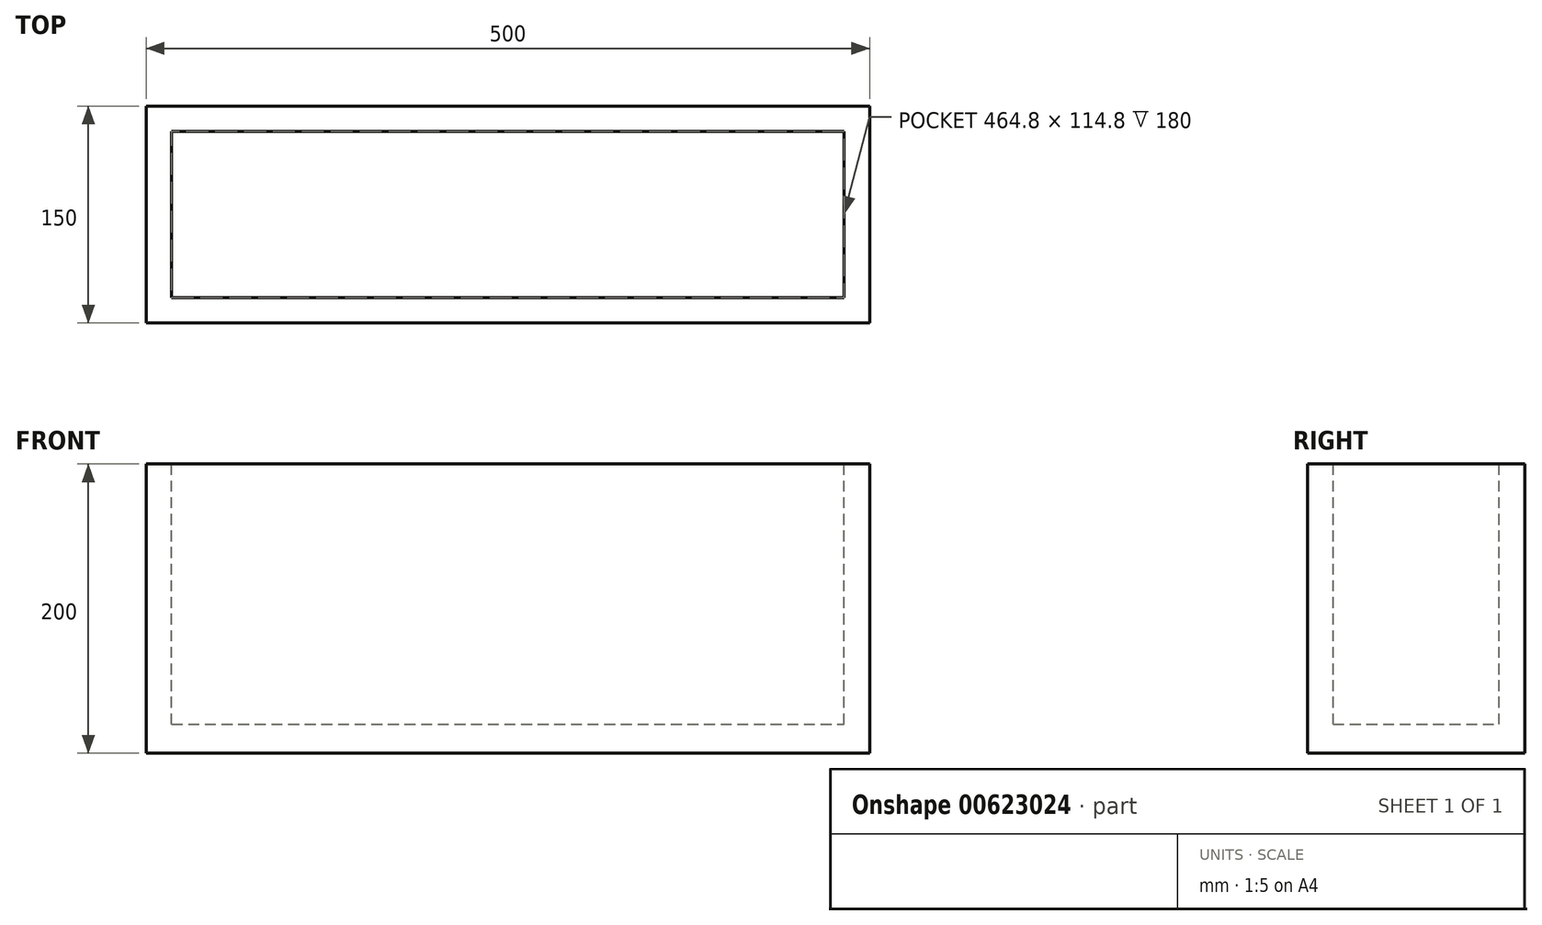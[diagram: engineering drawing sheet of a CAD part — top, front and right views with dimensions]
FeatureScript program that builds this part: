
annotation { "Feature Type Name" : "Feature", "Feature Type Description" : "" }
export const myFeature = defineFeature(function(context is Context, id is Id, definition is map)
    precondition{}
    {
        {
            var Q0;
            Q0=qCreatedBy(makeId("Top.planeOp"),FACE);
            var sketch = newSketch(context, id + "F0", { "sketchPlane" : qUnion([Q0])});
            skLineSegment(sketch, "E0.bottom", {"start": v(-187.75, -25.18) * mm, "end": v(312.25, -25.18) * mm});
            skLineSegment(sketch, "E0.top", {"start": v(-187.75, 124.82) * mm, "end": v(312.25, 124.82) * mm});
            skLineSegment(sketch, "E0.left", {"start": v(-187.75, -25.18) * mm, "end": v(-187.75, 124.82) * mm});
            skLineSegment(sketch, "E0.right", {"start": v(312.25, -25.18) * mm, "end": v(312.25, 124.82) * mm});
            skSolve(sketch);
        }
        {
            var Q0;
            Q0 = qSketchRegion(id + "F0", true);
            extrude(context, id + "F1", {"entities" : qUnion([Q0]), "depth" : 200 * mm, "offsetDistance" : 25 * mm});
        }
        {
            var Q0;
            Q0=makeQuery(id+"F1.opExtrude","CAP_FACE",FACE,{"disambiguationData":[OSD([sQuery(id+"F0.wireOp",EDGE,"E0.bottom"),sQuery(id+"F0.wireOp",EDGE,"E0.top"),sQuery(id+"F0.wireOp",EDGE,"E0.left"),sQuery(id+"F0.wireOp",EDGE,"E0.right")])],"isStart":false});
            var sketch = newSketch(context, id + "F2", { "sketchPlane" : qUnion([Q0])});
            skLineSegment(sketch, "E1.0", {"start": v(-170.15, -7.58) * mm, "end": v(-170.15, 107.22) * mm});
            skLineSegment(sketch, "E1.1", {"start": v(-170.15, -7.58) * mm, "end": v(294.65, -7.58) * mm});
            skLineSegment(sketch, "E1.2", {"start": v(294.65, -7.58) * mm, "end": v(294.65, 107.22) * mm});
            skLineSegment(sketch, "E1.3", {"start": v(-170.15, 107.22) * mm, "end": v(294.65, 107.22) * mm});
            skSolve(sketch);
        }
        {
            var Q0;
            Q0 = qSketchRegion(id + "F2", true);
            extrude(context, id + "F3", {"entities" : qUnion([Q0]), "operationType" : NewBodyOperationType.REMOVE, "oppositeDirection" : true, "depth" : 180 * mm, "offsetDistance" : 25 * mm});
        }
    });
